# Revit family: 2.Водяной нагреватель для круглых каналов WWK
name_source: partatom
category: Оборудование
revit_build: Autodesk Revit 2016 (Build: 20151209_0715(x64)
units: mm (PartAtom-declared; Revit-internal decimal feet)

## family parameters
Всегда вертикально = Да
На основе рабочей плоскости = Нет
Общий = Нет
При загрузке вырезать с полостями = Нет
Размер круглого соединителя = Использовать диаметр
Тип детали = Нормальный
Точка расчета площади = Нет

## types (4) — shared parameters
d = 13 мм
Единица измерения = шт.
Завод изготовитель = KORF
Ключевая пометка = Вентиляция
Материал = Сталь серая
Н = 105 мм
Наименование и тех.хар-ка = Водяной нагреватель для круглых каналов
Раздел = ОВ
отступ = 20 мм

## per-type parameters (varying)
| type | А | Д | Д1 | Е | Заправочный объем, л | К | Масса единицы | Теплопроизводительность, кВт | Тип, марка, обозначение |
| 160/2 | 270 мм | 160 мм | 157 мм | 203 мм | 0.4 м³ | 163 мм | 3,2 кг | 4 | WWK 160/2 |
| 200/2 | 295 мм | 200 мм | 196 мм | 226 мм | 0.45 м³ | 186 мм | 3,8 кг | 6.2 | WWK 200/2 |
| 250/2 | 345 мм | 250 мм | 245 мм | 276 мм | 0.62 м³ | 236 мм | 4.6 кг | 9.7 | WWK 250/2 |
| 315/2 | 420 мм | 315 мм | 309 мм | 353 мм | 0.95 м³ | 313 мм | 4.6 кг | 15.6 | WWK 315/2 |
